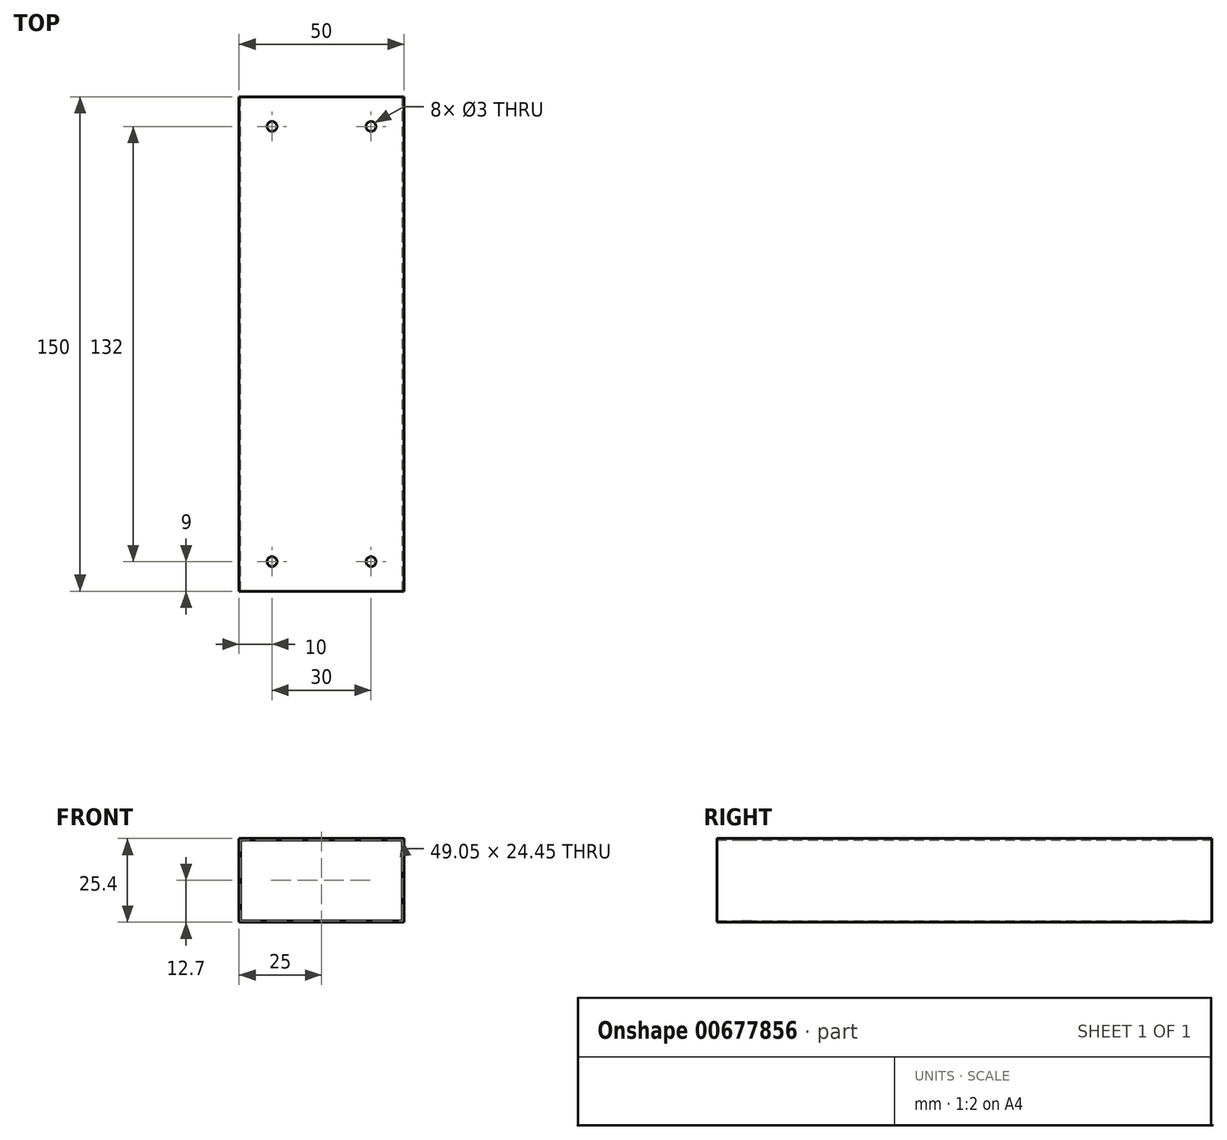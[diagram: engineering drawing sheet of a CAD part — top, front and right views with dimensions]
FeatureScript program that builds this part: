
annotation { "Feature Type Name" : "Feature", "Feature Type Description" : "" }
export const myFeature = defineFeature(function(context is Context, id is Id, definition is map)
    precondition{}
    {
        {
            var Q0;
            Q0=qCreatedBy(makeId("Front.planeOp"),FACE);
            var sketch = newSketch(context, id + "F0", { "sketchPlane" : qUnion([Q0])});
            skLineSegment(sketch, "E0.bottom", {"start": v(-25, 12.7) * mm, "end": v(25, 12.7) * mm});
            skLineSegment(sketch, "E0.top", {"start": v(-25, -12.7) * mm, "end": v(25, -12.7) * mm});
            skLineSegment(sketch, "E0.left", {"start": v(-25, 12.7) * mm, "end": v(-25, -12.7) * mm});
            skLineSegment(sketch, "E0.right", {"start": v(25, 12.7) * mm, "end": v(25, -12.7) * mm});
            skPoint(sketch, "E0.middle", {"position": v(0, 0) * mm});
            skLineSegment(sketch, "E1.bottom", {"start": v(-24.52, 12.22) * mm, "end": v(24.52, 12.22) * mm});
            skLineSegment(sketch, "E1.top", {"start": v(-24.52, -12.22) * mm, "end": v(24.52, -12.22) * mm});
            skLineSegment(sketch, "E1.left", {"start": v(-24.52, 12.22) * mm, "end": v(-24.52, -12.22) * mm});
            skLineSegment(sketch, "E1.right", {"start": v(24.52, 12.22) * mm, "end": v(24.52, -12.22) * mm});
            skPoint(sketch, "E2.visualSharp", {"position": v(-24.52, 12.22) * mm});
            skLineSegment(sketch, "E2.filletArc", {"start": v(-24.52, 12.22) * mm, "end": v(-24.52, 12.22) * mm});
            skPoint(sketch, "E3.visualSharp", {"position": v(24.52, 12.22) * mm});
            skLineSegment(sketch, "E3.filletArc", {"start": v(24.52, 12.22) * mm, "end": v(24.52, 12.22) * mm});
            skPoint(sketch, "E4.visualSharp", {"position": v(24.52, -12.22) * mm});
            skLineSegment(sketch, "E4.filletArc", {"start": v(24.52, -12.22) * mm, "end": v(24.52, -12.22) * mm});
            skPoint(sketch, "E5.visualSharp", {"position": v(-24.52, -12.22) * mm});
            skLineSegment(sketch, "E5.filletArc", {"start": v(-24.52, -12.22) * mm, "end": v(-24.52, -12.22) * mm});
            skPoint(sketch, "E6.visualSharp", {"position": v(-25, 12.7) * mm});
            skLineSegment(sketch, "E6.filletArc", {"start": v(-25, 12.7) * mm, "end": v(-25, 12.7) * mm});
            skPoint(sketch, "E7.visualSharp", {"position": v(25, 12.7) * mm});
            skLineSegment(sketch, "E7.filletArc", {"start": v(25, 12.7) * mm, "end": v(25, 12.7) * mm});
            skPoint(sketch, "E8.visualSharp", {"position": v(25, -12.7) * mm});
            skLineSegment(sketch, "E8.filletArc", {"start": v(25, -12.7) * mm, "end": v(25, -12.7) * mm});
            skPoint(sketch, "E9.visualSharp", {"position": v(-25, -12.7) * mm});
            skLineSegment(sketch, "E9.filletArc", {"start": v(-25, -12.7) * mm, "end": v(-25, -12.7) * mm});
            skSolve(sketch);
        }
        {
            var Q0;
            Q0=makeQuery(id+"F0.imprint","IMPRINT",FACE,{"disambiguationData":[TD([[makeQuery(id+"F0.imprint","IMPRINT",EDGE,{"derivedFrom":sQuery(id+"F0.wireOp",EDGE,"E0.bottom")}),-1.0]])]});
            extrude(context, id + "F1", {"entities" : qUnion([Q0]), "depth" : 150 * mm, "offsetDistance" : 25 * mm});
        }
        {
            var Q0;
            Q0=qCreatedBy(makeId("Top.planeOp"),FACE);
            var sketch = newSketch(context, id + "F2", { "sketchPlane" : qUnion([Q0])});
            skCircle(sketch, "E10", {"center": v(-15, -9) * mm, "radius": 1.5 * mm});
            skCircle(sketch, "E11", {"center": v(15, -9) * mm, "radius": 1.5 * mm});
            skCircle(sketch, "E12", {"center": v(-15, -141) * mm, "radius": 1.5 * mm});
            skCircle(sketch, "E13", {"center": v(15, -141) * mm, "radius": 1.5 * mm});
            skSolve(sketch);
        }
        {
            var Q0;
            Q0=makeQuery(id+"F2.imprint","IMPRINT",FACE,{"disambiguationData":[TD([[makeQuery(id+"F2.imprint","IMPRINT",EDGE,{"derivedFrom":sQuery(id+"F2.wireOp",EDGE,"E10")}),1.0]])]});
            extrude(context, id + "F3", {"entities" : qUnion([Q0]), "operationType" : NewBodyOperationType.REMOVE, "endBound" : BoundingType.SYMMETRIC, "oppositeDirection" : true, "depth" : 30 * mm, "offsetDistance" : 25 * mm});
        }
        {
            var Q0;
            Q0=makeQuery(id+"F2.imprint","IMPRINT",FACE,{"disambiguationData":[TD([[makeQuery(id+"F2.imprint","IMPRINT",EDGE,{"derivedFrom":sQuery(id+"F2.wireOp",EDGE,"E11")}),1.0]])]});
            extrude(context, id + "F4", {"entities" : qUnion([Q0]), "operationType" : NewBodyOperationType.REMOVE, "endBound" : BoundingType.SYMMETRIC, "oppositeDirection" : true, "depth" : 30 * mm, "offsetDistance" : 25 * mm});
        }
        {
            var Q0;
            Q0=makeQuery(id+"F2.imprint","IMPRINT",FACE,{"disambiguationData":[TD([[makeQuery(id+"F2.imprint","IMPRINT",EDGE,{"derivedFrom":sQuery(id+"F2.wireOp",EDGE,"E13")}),1.0]])]});
            var Q1;
            Q1=makeQuery(id+"F2.imprint","IMPRINT",FACE,{"disambiguationData":[TD([[makeQuery(id+"F2.imprint","IMPRINT",EDGE,{"derivedFrom":sQuery(id+"F2.wireOp",EDGE,"E12")}),1.0]])]});
            extrude(context, id + "F5", {"entities" : qUnion([Q0, Q1]), "operationType" : NewBodyOperationType.REMOVE, "endBound" : BoundingType.SYMMETRIC, "oppositeDirection" : true, "depth" : 30 * mm, "offsetDistance" : 25 * mm});
        }
    });
